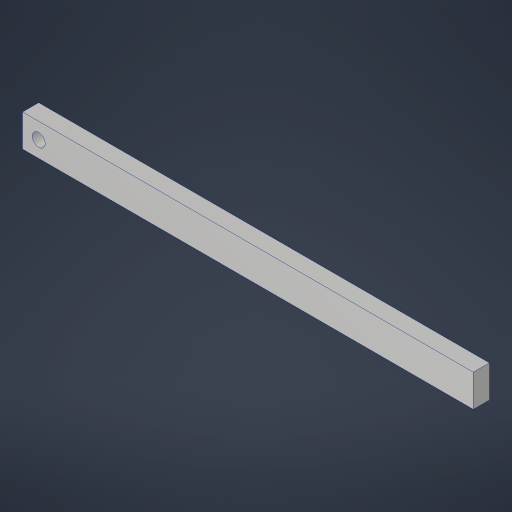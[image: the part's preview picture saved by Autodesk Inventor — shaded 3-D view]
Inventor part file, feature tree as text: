
AUTODESK INVENTOR PART (.ipt)
format: ipt  version: 2023.4 (Build 274418000, 418)  size: 167,936 bytes
history: native  units: in
note: dims shown in document units (in); Inventor stores cm internally (conversion verified against a paired STEP export)
features: sketch x1, extrude x1, hole x1
ambient origin geometry x8: Origin, YZ Plane, XZ Plane, XY Plane, X Axis, Y Axis, Z Axis, Center Point
bodies: Solid1 (feature_tree)
feature tree (3):
  sketch  "Sketch1"  dims[d0=7.0in d1=0.5in d2=0.25in d3=0.25in d4=0.0in d5=0.201in d6=0.75in d7=0.385in d8=0.25in d9=0.5635in d10=1.0in d11=0.8108in]
  extrude  "Extrusion1"  Depth=0.5in
  hole  "Hole1"  [1 undecoded]
note: 1 required parameter value undecoded (feature->parameter linkage not recoverable at this tier; creation-order binding heuristic only, values carry confidence <= 0.55)
